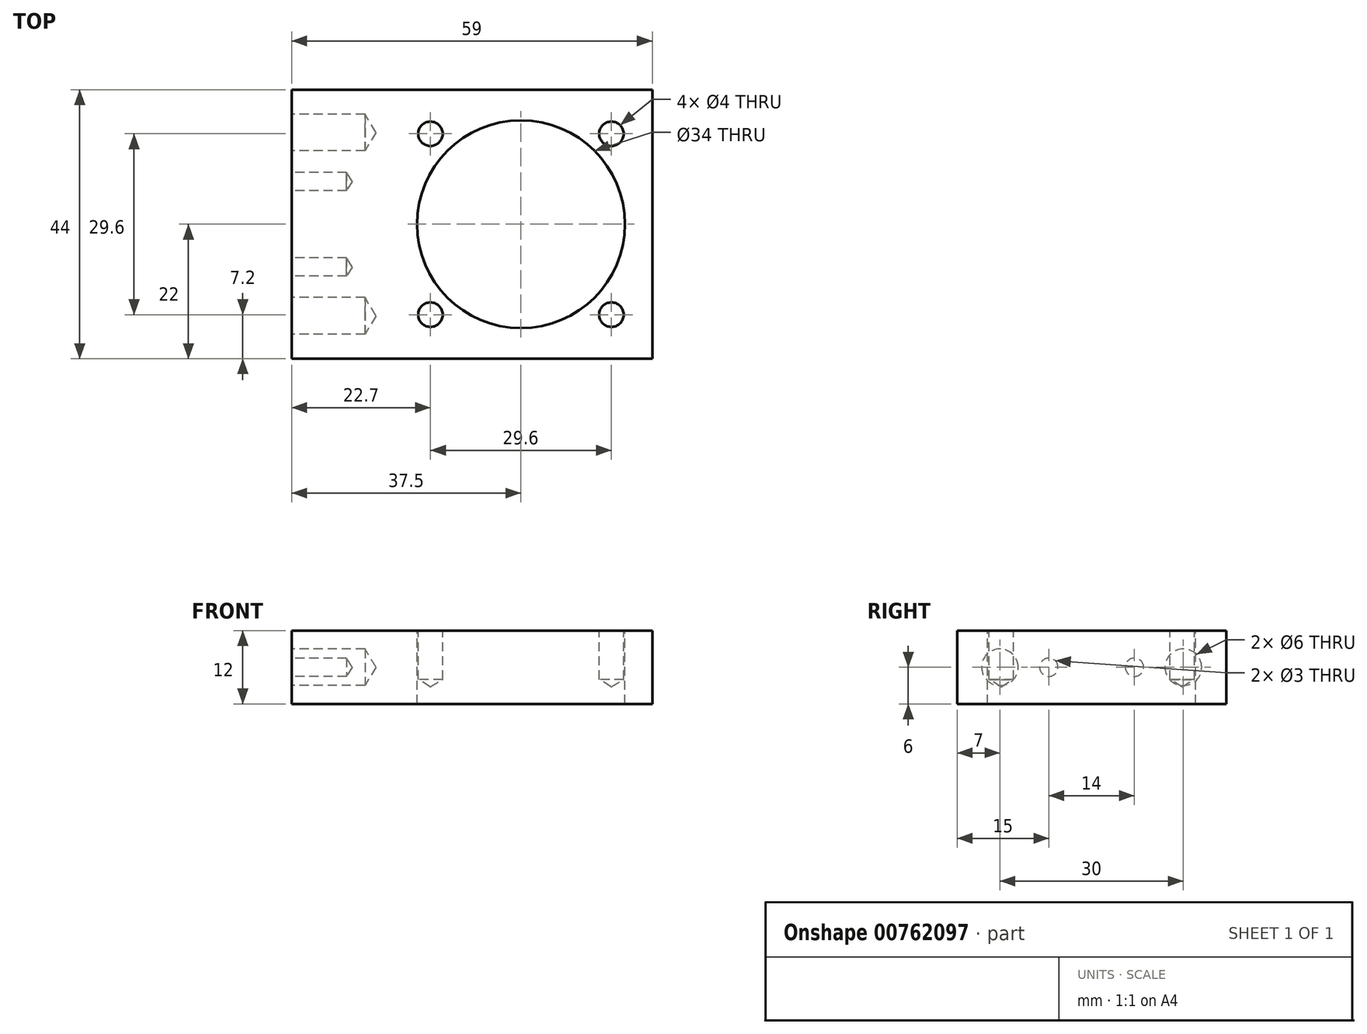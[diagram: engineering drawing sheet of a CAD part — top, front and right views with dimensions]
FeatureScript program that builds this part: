
annotation { "Feature Type Name" : "Feature", "Feature Type Description" : "" }
export const myFeature = defineFeature(function(context is Context, id is Id, definition is map)
    precondition{}
    {
        {
            var Q0;
            Q0=qCreatedBy(makeId("Top.planeOp"),FACE);
            var sketch = newSketch(context, id + "F0", { "sketchPlane" : qUnion([Q0])});
            skLineSegment(sketch, "E0.bottom", {"start": v(0, 22) * mm, "end": v(59, 22) * mm});
            skLineSegment(sketch, "E0.top", {"start": v(0, -22) * mm, "end": v(59, -22) * mm});
            skLineSegment(sketch, "E0.left", {"start": v(0, 22) * mm, "end": v(0, -22) * mm});
            skLineSegment(sketch, "E0.right", {"start": v(59, 22) * mm, "end": v(59, -22) * mm});
            skSolve(sketch);
        }
        {
            var Q0;
            Q0 = qSketchRegion(id + "F0", true);
            extrude(context, id + "F1", {"entities" : qUnion([Q0]), "depth" : 12 * mm, "offsetDistance" : 25 * mm});
        }
        {
            var Q0;
            Q0=makeQuery(id+"F1.opExtrude","CAP_FACE",FACE,{"disambiguationData":[OSD([sQuery(id+"F0.wireOp",EDGE,"E0.bottom"),sQuery(id+"F0.wireOp",EDGE,"E0.top"),sQuery(id+"F0.wireOp",EDGE,"E0.left"),sQuery(id+"F0.wireOp",EDGE,"E0.right")])],"isStart":false});
            var sketch = newSketch(context, id + "F2", { "sketchPlane" : qUnion([Q0])});
            skPoint(sketch, "E1", {"position": v(37.5, 0) * mm});
            skSolve(sketch);
        }
        {
            var Q0;
            Q0=sQuery(id+"F2.wireOp",VERTEX,"E1");
            var Q1;
            Q1=makeQuery(id+"F1.opExtrude","SWEPT_BODY",BODY,{"disambiguationData":[OSD([sQuery(id+"F0.wireOp",EDGE,"E0.bottom"),sQuery(id+"F0.wireOp",EDGE,"E0.top"),sQuery(id+"F0.wireOp",EDGE,"E0.left"),sQuery(id+"F0.wireOp",EDGE,"E0.right")])]});
            hole(context, id + "F3", {"style" : HoleStyle.SIMPLE, "endStyle" : HoleEndStyle.BLIND, "holeDiameter" : 34 * mm, "majorDiameter" : 5 * mm, "holeDepth" : 20 * mm, "isTappedThrough" : true, "tappedDepth" : 11.5 * mm, "tapClearance" : 3, "locations" : qUnion([Q0]), "scope" : qUnion([Q1])});
        }
        {
            var Q0;
            Q0=makeQuery(id+"F1.opExtrude","CAP_FACE",FACE,{"disambiguationData":[OSD([sQuery(id+"F0.wireOp",EDGE,"E0.bottom"),sQuery(id+"F0.wireOp",EDGE,"E0.top"),sQuery(id+"F0.wireOp",EDGE,"E0.left"),sQuery(id+"F0.wireOp",EDGE,"E0.right")])],"isStart":false});
            var sketch = newSketch(context, id + "F4", { "sketchPlane" : qUnion([Q0])});
            skPoint(sketch, "E2", {"position": v(22.7, 14.8) * mm});
            skPoint(sketch, "E3", {"position": v(52.3, 14.8) * mm});
            skPoint(sketch, "E4", {"position": v(52.3, -14.8) * mm});
            skPoint(sketch, "E5", {"position": v(22.7, -14.8) * mm});
            skSolve(sketch);
        }
        {
            var Q0;
            Q0=sQuery(id+"F4.wireOp",VERTEX,"E3");
            var Q1;
            Q1=sQuery(id+"F4.wireOp",VERTEX,"E4");
            var Q2;
            Q2=sQuery(id+"F4.wireOp",VERTEX,"E5");
            var Q3;
            Q3=sQuery(id+"F4.wireOp",VERTEX,"E2");
            var Q4;
            Q4=makeQuery(id+"F1.opExtrude","SWEPT_BODY",BODY,{"disambiguationData":[OSD([sQuery(id+"F0.wireOp",EDGE,"E0.bottom"),sQuery(id+"F0.wireOp",EDGE,"E0.top"),sQuery(id+"F0.wireOp",EDGE,"E0.left"),sQuery(id+"F0.wireOp",EDGE,"E0.right")])]});
            hole(context, id + "F5", {"style" : HoleStyle.SIMPLE, "endStyle" : HoleEndStyle.BLIND, "holeDiameter" : 4 * mm, "majorDiameter" : 5 * mm, "holeDepth" : 8 * mm, "isTappedThrough" : true, "tappedDepth" : 11.5 * mm, "tapClearance" : 3, "locations" : qUnion([Q0, Q1, Q2, Q3]), "scope" : qUnion([Q4])});
        }
        {
            var Q0;
            Q0=makeQuery(id+"F1.opExtrude","SWEPT_FACE",FACE,{"disambiguationData":[OSD([sQuery(id+"F0.wireOp",EDGE,"E0.left")])]});
            var sketch = newSketch(context, id + "F6", { "sketchPlane" : qUnion([Q0])});
            skPoint(sketch, "E6", {"position": v(-15, 6) * mm});
            skPoint(sketch, "E7", {"position": v(15, 6) * mm});
            skSolve(sketch);
        }
        {
            var Q0;
            Q0=sQuery(id+"F6.wireOp",VERTEX,"E6");
            var Q1;
            Q1=sQuery(id+"F6.wireOp",VERTEX,"E7");
            var Q2;
            Q2=makeQuery(id+"F1.opExtrude","SWEPT_BODY",BODY,{"disambiguationData":[OSD([sQuery(id+"F0.wireOp",EDGE,"E0.bottom"),sQuery(id+"F0.wireOp",EDGE,"E0.top"),sQuery(id+"F0.wireOp",EDGE,"E0.left"),sQuery(id+"F0.wireOp",EDGE,"E0.right")])]});
            hole(context, id + "F7", {"style" : HoleStyle.SIMPLE, "endStyle" : HoleEndStyle.BLIND, "holeDiameter" : 6 * mm, "majorDiameter" : 5 * mm, "holeDepth" : 12 * mm, "isTappedThrough" : true, "tappedDepth" : 11.5 * mm, "tapClearance" : 3, "locations" : qUnion([Q0, Q1]), "scope" : qUnion([Q2])});
        }
        {
            var Q0;
            Q0=makeQuery(id+"F1.opExtrude","SWEPT_FACE",FACE,{"disambiguationData":[OSD([sQuery(id+"F0.wireOp",EDGE,"E0.left")])]});
            var sketch = newSketch(context, id + "F8", { "sketchPlane" : qUnion([Q0])});
            skPoint(sketch, "E8", {"position": v(-7, 6) * mm});
            skPoint(sketch, "E9", {"position": v(7, 6) * mm});
            skSolve(sketch);
        }
        {
            var Q0;
            Q0=sQuery(id+"F8.wireOp",VERTEX,"E8");
            var Q1;
            Q1=sQuery(id+"F8.wireOp",VERTEX,"E9");
            var Q2;
            Q2=makeQuery(id+"F1.opExtrude","SWEPT_BODY",BODY,{"disambiguationData":[OSD([sQuery(id+"F0.wireOp",EDGE,"E0.bottom"),sQuery(id+"F0.wireOp",EDGE,"E0.top"),sQuery(id+"F0.wireOp",EDGE,"E0.left"),sQuery(id+"F0.wireOp",EDGE,"E0.right")])]});
            hole(context, id + "F9", {"style" : HoleStyle.SIMPLE, "endStyle" : HoleEndStyle.BLIND, "holeDiameter" : 3 * mm, "majorDiameter" : 5 * mm, "holeDepth" : 9 * mm, "isTappedThrough" : true, "tappedDepth" : 11.5 * mm, "tapClearance" : 3, "locations" : qUnion([Q0, Q1]), "scope" : qUnion([Q2])});
        }
    });
